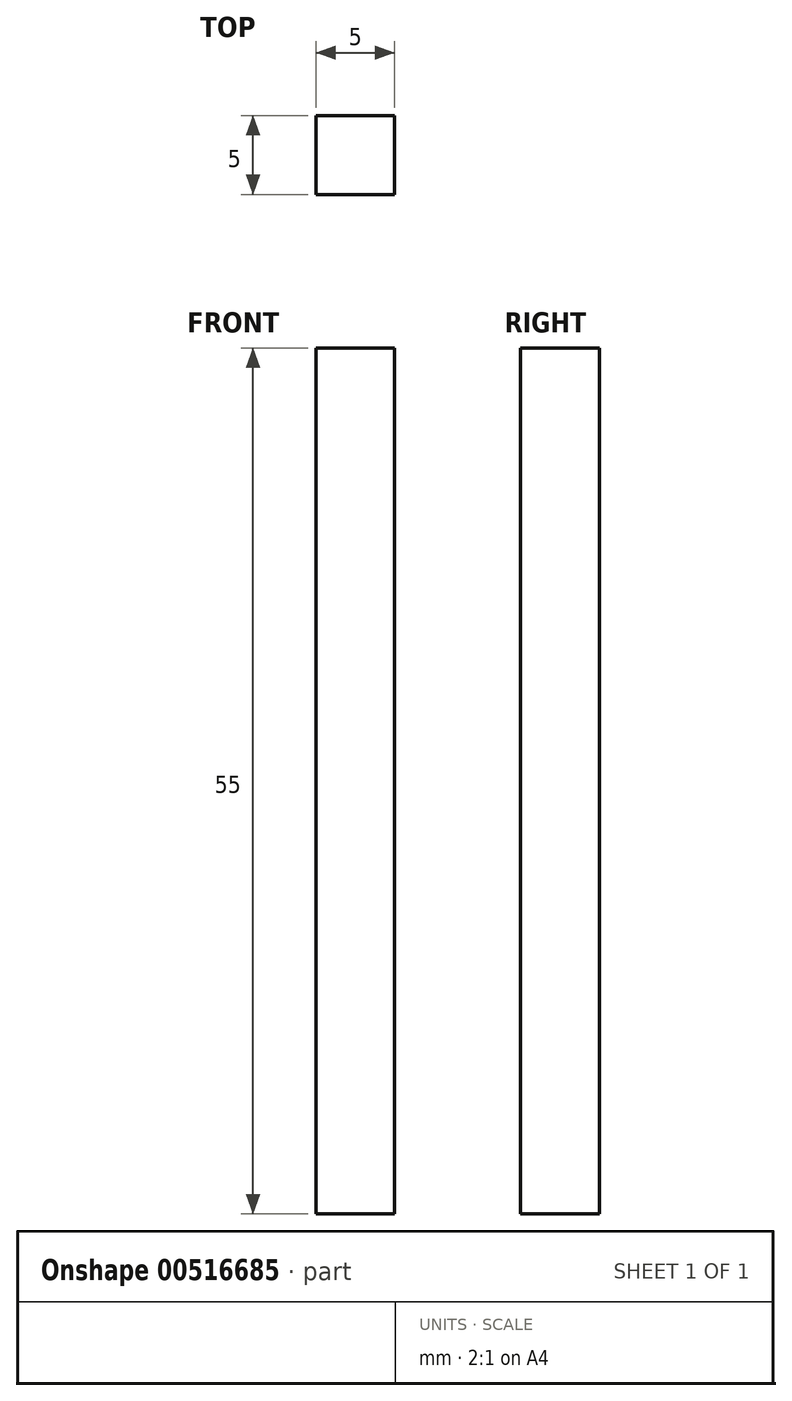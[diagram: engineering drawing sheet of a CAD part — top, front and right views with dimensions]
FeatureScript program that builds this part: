
annotation { "Feature Type Name" : "Feature", "Feature Type Description" : "" }
export const myFeature = defineFeature(function(context is Context, id is Id, definition is map)
    precondition{}
    {
        {
            var Q0;
            Q0=qCreatedBy(makeId("Front.planeOp"),FACE);
            var sketch = newSketch(context, id + "F0", { "sketchPlane" : qUnion([Q0])});
            skLineSegment(sketch, "E0.bottom", {"start": v(2.5, -27.5) * mm, "end": v(-2.5, -27.5) * mm});
            skLineSegment(sketch, "E0.top", {"start": v(2.5, 27.5) * mm, "end": v(-2.5, 27.5) * mm});
            skLineSegment(sketch, "E0.left", {"start": v(2.5, -27.5) * mm, "end": v(2.5, 27.5) * mm});
            skLineSegment(sketch, "E0.right", {"start": v(-2.5, -27.5) * mm, "end": v(-2.5, 27.5) * mm});
            skPoint(sketch, "E0.middle", {"position": v(0, 0) * mm});
            skLineSegment(sketch, "E1", {"start": v(-2, -34.5) * mm, "end": v(2, -34.5) * mm});
            skPoint(sketch, "E2", {"position": v(0, -27.5) * mm});
            skPoint(sketch, "E3", {"position": v(0, -34.5) * mm});
            skLineSegment(sketch, "E4", {"start": v(-2.5, -27.5) * mm, "end": v(-2, -34.5) * mm});
            skLineSegment(sketch, "E5", {"start": v(2.5, -27.5) * mm, "end": v(2, -34.5) * mm});
            skPoint(sketch, "E6", {"position": v(-1, -34.5) * mm});
            skPoint(sketch, "E7", {"position": v(1, -34.5) * mm});
            skLineSegment(sketch, "E8", {"start": v(-1, -34.5) * mm, "end": v(-1, -54.5) * mm});
            skLineSegment(sketch, "E9", {"start": v(-1, -54.5) * mm, "end": v(1, -54.5) * mm});
            skLineSegment(sketch, "E10", {"start": v(1, -54.5) * mm, "end": v(1, -34.5) * mm});
            skLineSegment(sketch, "E11", {"start": v(-1, -54.5) * mm, "end": v(0, -57.51) * mm});
            skLineSegment(sketch, "E12", {"start": v(1, -54.5) * mm, "end": v(0, -57.51) * mm});
            skSolve(sketch);
        }
        {
            var Q0;
            Q0=makeQuery(id+"F0.imprint","IMPRINT",FACE,{"disambiguationData":[TD([[makeQuery(id+"F0.imprint","IMPRINT",EDGE,{"derivedFrom":sQuery(id+"F0.wireOp",EDGE,"E0.top")}),1.0]])]});
            extrude(context, id + "F1", {"entities" : qUnion([Q0]), "depth" : 2.5 * mm, "offsetDistance" : 25 * mm, "hasSecondDirection" : true, "secondDirectionOppositeDirection" : true, "secondDirectionDepth" : 2.5 * mm});
        }
        {
            var Q0;
            Q0=qCreatedBy(makeId("Right.planeOp"),FACE);
            var sketch = newSketch(context, id + "F2", { "sketchPlane" : qUnion([Q0])});
            skLineSegment(sketch, "E13.bottom", {"start": v(2.5, -27.5) * mm, "end": v(-2.5, -27.5) * mm});
            skLineSegment(sketch, "E13.top", {"start": v(2.5, 27.5) * mm, "end": v(-2.5, 27.5) * mm});
            skLineSegment(sketch, "E13.left", {"start": v(2.5, -27.5) * mm, "end": v(2.5, 27.5) * mm});
            skLineSegment(sketch, "E13.right", {"start": v(-2.5, -27.5) * mm, "end": v(-2.5, 27.5) * mm});
            skPoint(sketch, "E13.middle", {"position": v(0, 0) * mm});
            skLineSegment(sketch, "E14", {"start": v(-2, -34.5) * mm, "end": v(2, -34.5) * mm});
            skPoint(sketch, "E15", {"position": v(0, -27.5) * mm});
            skPoint(sketch, "E16", {"position": v(0, -34.5) * mm});
            skLineSegment(sketch, "E17", {"start": v(-2.5, -27.5) * mm, "end": v(-2, -34.5) * mm});
            skLineSegment(sketch, "E18", {"start": v(2.5, -27.5) * mm, "end": v(2, -34.5) * mm});
            skPoint(sketch, "E19", {"position": v(-1, -34.5) * mm});
            skPoint(sketch, "E20", {"position": v(1, -34.5) * mm});
            skLineSegment(sketch, "E21", {"start": v(-1, -34.5) * mm, "end": v(-1, -54.5) * mm});
            skLineSegment(sketch, "E22", {"start": v(-1, -54.5) * mm, "end": v(1, -54.5) * mm});
            skLineSegment(sketch, "E23", {"start": v(1, -54.5) * mm, "end": v(1, -34.5) * mm});
            skLineSegment(sketch, "E24", {"start": v(-1, -54.5) * mm, "end": v(0, -57.51) * mm});
            skLineSegment(sketch, "E25", {"start": v(1, -54.5) * mm, "end": v(0, -57.51) * mm});
            skSolve(sketch);
        }
        {
            var Q0;
            Q0=makeQuery(id+"F2.imprint","IMPRINT",FACE,{"disambiguationData":[TD([[makeQuery(id+"F2.imprint","IMPRINT",EDGE,{"derivedFrom":sQuery(id+"F2.wireOp",EDGE,"E13.bottom")}),1.0]])]});
            var Q1;
            Q1=makeQuery(id+"F0.imprint","IMPRINT",FACE,{"disambiguationData":[TD([[makeQuery(id+"F0.imprint","IMPRINT",EDGE,{"derivedFrom":sQuery(id+"F0.wireOp",EDGE,"E0.bottom")}),1.0]])]});
            var Q2;
            Q2=sQuery(id+"F0.wireOp",EDGE,"E4");
            var Q3;
            Q3=sQuery(id+"F0.wireOp",EDGE,"E5");
            var Q4;
            Q4=sQuery(id+"F0.wireOp",EDGE,"E1");
            extrude(context, id + "F3", {"entities" : qUnion([Q0, Q1]), "bodyType" : ToolBodyType.SURFACE, "surfaceEntities" : qUnion([Q2, Q3, Q4]), "depth" : 0.1 * mm, "offsetDistance" : 25 * mm});
        }
    });
